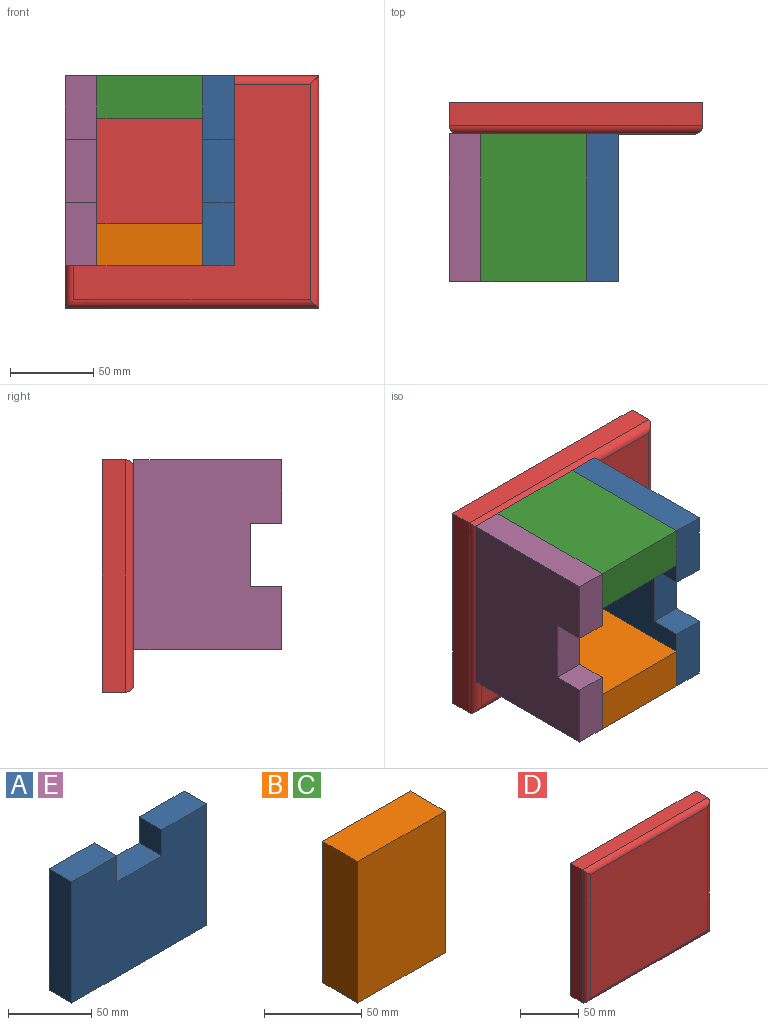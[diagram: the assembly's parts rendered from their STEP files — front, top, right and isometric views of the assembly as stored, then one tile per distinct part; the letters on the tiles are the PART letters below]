
ASSEMBLY  parts=5 mates=11
PART A: 10 faces, bbox 114.3x19.1x88.9 mm
  f0: plane 38.1x19.05mm, normal (0,0,1), area 725.8mm2, adj f1,f7,f8,f9
  f1: plane 88.9x19.05mm, normal (-1,0,0), area 1693.5mm2, adj f0,f2,f8,f9
  f2: plane 114.3x19.05mm, normal (0,0,-1), area 2177.4mm2, adj f1,f3,f8,f9
  f3: plane 88.9x19.05mm, normal (1,0,0), area 1693.5mm2, adj f2,f4,f8,f9
  f4: plane 38.1x19.05mm, normal (0,0,1), area 725.8mm2, adj f3,f5,f8,f9
  f5: plane 19.05x19.05mm, normal (-1,0,0), area 362.9mm2, adj f4,f6,f8,f9
  f6: plane 38.1x19.05mm, normal (0,0,1), area 725.8mm2, adj f5,f7,f8,f9
  f7: plane 19.05x19.05mm, normal (1,0,0), area 362.9mm2, adj f0,f6,f8,f9
  f8: plane 114.3x88.9mm, normal (0,-1,0), area 9435.5mm2, adj f0,f1,f2,f3,f4,f5,f6,f7
  f9: plane 114.3x88.9mm, normal (0,1,0), area 9435.5mm2, adj f0,f1,f2,f3,f4,f5,f6,f7
PART B: 6 faces, bbox 63.5x25.4x88.9 mm
  f0: plane 63.5x25.4mm, normal (0,0,1), area 1612.9mm2, adj f1,f3,f4,f5
  f1: plane 88.9x25.4mm, normal (-1,0,0), area 2258.1mm2, adj f0,f2,f4,f5
  f2: plane 63.5x25.4mm, normal (0,0,-1), area 1612.9mm2, adj f1,f3,f4,f5
  f3: plane 88.9x25.4mm, normal (1,0,0), area 2258.1mm2, adj f0,f2,f4,f5
  f4: plane 88.9x63.5mm, normal (0,-1,0), area 5645.2mm2, adj f0,f1,f2,f3
  f5: plane 88.9x63.5mm, normal (0,1,0), area 5645.2mm2, adj f0,f1,f2,f3
PART C: same geometry as B
PART D: 10 faces, bbox 152.4x19.1x139.7 mm
  f0: plane 152.4x13.97mm, normal (0,0,1), area 2129mm2, adj f1,f3,f5,f6
  f1: plane 139.7x13.97mm, normal (-1,0,0), area 1951.6mm2, adj f0,f2,f5,f7
  f2: plane 152.4x13.97mm, normal (0,0,-1), area 2129mm2, adj f1,f3,f5,f9
  f3: plane 139.7x13.97mm, normal (1,0,0), area 1951.6mm2, adj f0,f2,f5,f8
  f4: plane 142.24x129.54mm, normal (0,-1,0), area 18425.8mm2, adj f6,f7,f8,f9
  f5: plane 152.4x139.7mm, normal (0,1,0), area 21290.3mm2, adj f0,f1,f2,f3
  f6: cylinder r=5.08mm len=152.4mm, axis (1,0,0), area 1186.6mm2, adj f0,f4,f7,f8
  f7: cylinder r=5.08mm len=139.7mm, axis (0,0,1), area 1085.3mm2, adj f1,f4,f6,f9
  f8: cylinder r=5.08mm len=139.7mm, axis (0,0,-1), area 1085.3mm2, adj f3,f4,f6,f9
  f9: cylinder r=5.08mm len=152.4mm, axis (-1,0,0), area 1186.6mm2, adj f2,f4,f7,f8
PART E: same geometry as A
PLACE A rot(axis=(0.58,0.58,-0.58),120deg) t=(121,-163.92,-193.53)mm
PLACE B rot(axis=(1,0,0),90deg) t=(108.3,-160.6,-208.88)mm
PLACE C rot(axis=(-1,0,0),90deg) t=(108.3,-167.65,-145.38)mm
PLACE D t=(120.9,-100.63,-192.42)mm
PLACE E rot(axis=(0.58,0.58,-0.58),120deg) t=(38.45,-163.92,-193.53)mm
MATE planar A.f8 <-> C.f3  axis (-1,0,0) through (101.95,-161.44,-177.13)mm
MATE planar C.f2 <-> A.f0  axis (0,-1,0) through (70.2,-208.58,-132.68)mm
MATE planar D.f0 <-> C.f4  axis (0,0,1) through (95.6,-107.61,-119.98)mm
MATE planar C.f4 <-> A.f1  axis (0,0,1) through (70.2,-164.13,-119.98)mm
MATE planar D.f4 <-> C.f0  axis (0,-1,0) through (95.6,-119.68,-189.83)mm
MATE planar E.f1 <-> C.f4  axis (0,0,1) through (28.93,-164.13,-119.98)mm
MATE planar E.f9 <-> B.f1  axis (1,0,0) through (38.45,-161.44,-177.13)mm
MATE planar E.f4 <-> B.f0  axis (0,-1,0) through (28.93,-208.58,-215.23)mm
MATE planar E.f8 <-> D.f1  axis (-1,0,0) through (19.4,-161.44,-177.13)mm
MATE planar B.f4 <-> A.f3  axis (0,0,-1) through (70.2,-164.13,-234.28)mm
MATE planar B.f3 <-> A.f8  axis (1,0,0) through (101.95,-164.13,-221.58)mm
